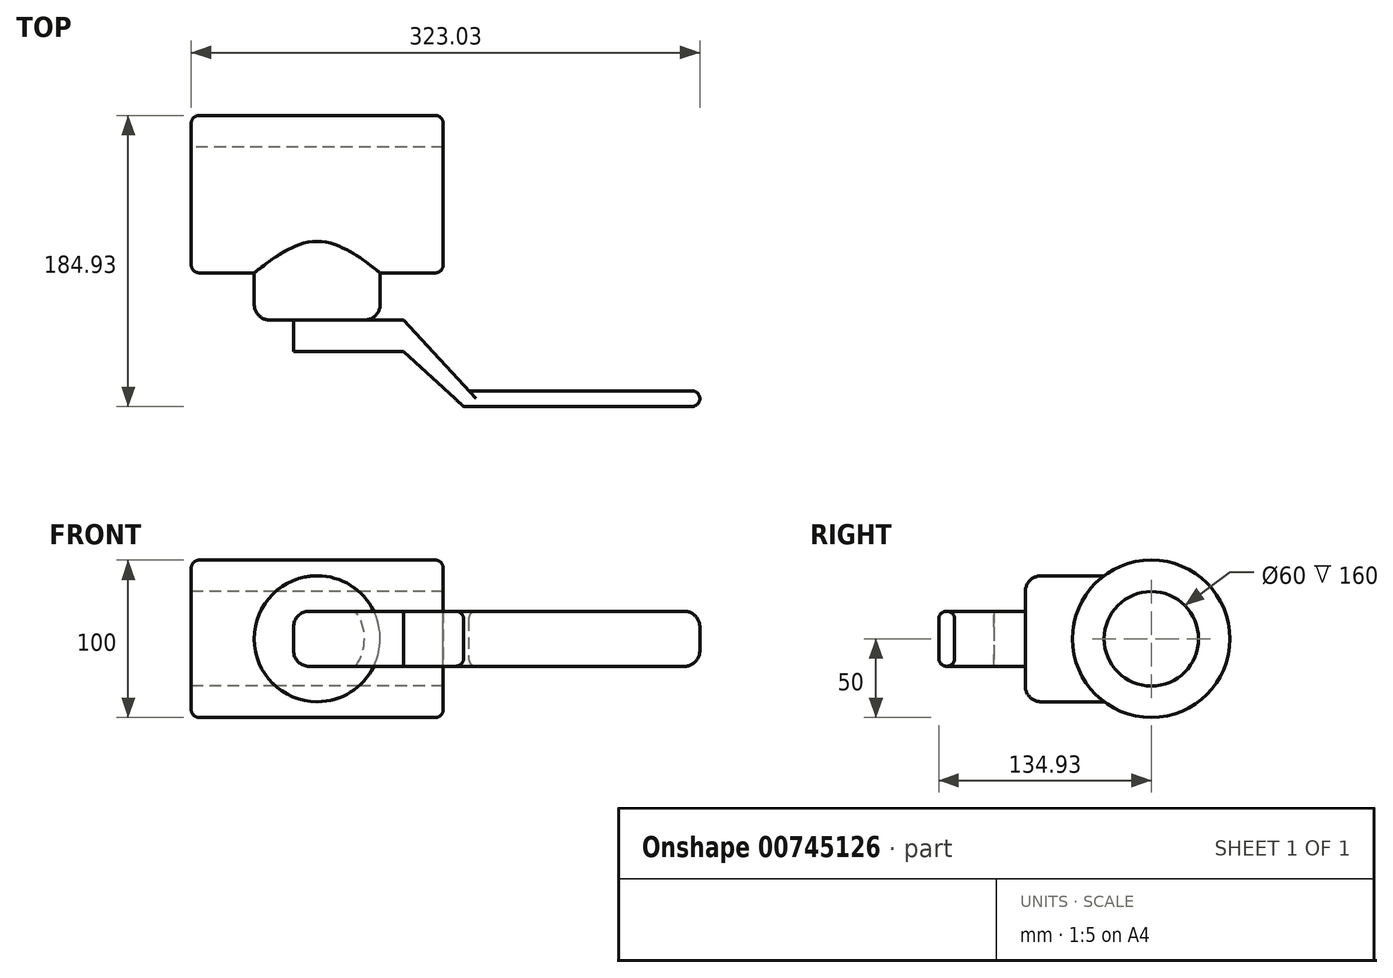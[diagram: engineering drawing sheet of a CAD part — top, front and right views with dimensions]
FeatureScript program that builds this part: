
annotation { "Feature Type Name" : "Feature", "Feature Type Description" : "" }
export const myFeature = defineFeature(function(context is Context, id is Id, definition is map)
    precondition{}
    {
        {
            var Q0;
            Q0=qCreatedBy(makeId("Right.planeOp"),FACE);
            var sketch = newSketch(context, id + "F0", { "sketchPlane" : qUnion([Q0])});
            skCircle(sketch, "E0", {"center": v(0, 0) * mm, "radius": 30 * mm});
            skCircle(sketch, "E1", {"center": v(0, 0) * mm, "radius": 50 * mm});
            skSolve(sketch);
        }
        {
            var Q0;
            Q0=makeQuery(id+"F0.imprint","IMPRINT",FACE,{"disambiguationData":[TD([[makeQuery(id+"F0.imprint","IMPRINT",EDGE,{"derivedFrom":sQuery(id+"F0.wireOp",EDGE,"E0")}),-1.0]])]});
            extrude(context, id + "F1", {"entities" : qUnion([Q0]), "depth" : 160 * mm, "offsetDistance" : 25 * mm});
        }
        {
            var Q0;
            Q0=qCreatedBy(makeId("Front.planeOp"),FACE);
            var sketch = newSketch(context, id + "F2", { "sketchPlane" : qUnion([Q0])});
            skCircle(sketch, "E2", {"center": v(80, 0) * mm, "radius": 40 * mm});
            skSolve(sketch);
        }
        {
            var Q0;
            Q0=makeQuery(id+"F2.imprint","IMPRINT",FACE,{"disambiguationData":[TD([[makeQuery(id+"F2.imprint","IMPRINT",EDGE,{"derivedFrom":sQuery(id+"F2.wireOp",EDGE,"E2")}),1.0]])]});
            var Q1;
            Q1=sQuery(id+"F2.wireOp",EDGE,"E2");
            var Q2;
            Q2=makeQuery(id+"F1.opExtrude","SWEPT_BODY",BODY,{"disambiguationData":[OSD([sQuery(id+"F0.wireOp",EDGE,"E0"),sQuery(id+"F0.wireOp",EDGE,"E1")])]});
            extrude(context, id + "F3", {"entities" : qUnion([Q0]), "operationType" : NewBodyOperationType.ADD, "surfaceEntities" : qUnion([Q1]), "depth" : 80 * mm, "offsetDistance" : 25 * mm, "hasSecondDirection" : true, "secondDirectionBound" : SecondDirectionBoundingType.UP_TO_BODY, "secondDirectionOppositeDirection" : false, "secondDirectionDepth" : 25 * mm, "secondDirectionBoundEntityBody" : qUnion([Q2])});
        }
        {
            var Q0;
            Q0=makeQuery(id+"F3.opExtrude","CAP_EDGE",EDGE,{"disambiguationData":[OSD([sQuery(id+"F2.wireOp",EDGE,"E2")])],"isStart":false});
            fillet(context, id + "F4", {"entities" : qUnion([Q0]), "radius" : 10 * mm, "tangentPropagation" : true, "allowEdgeOverflow" : false});
        }
        {
            var Q0;
            Q0=qCreatedBy(makeId("Top.planeOp"),FACE);
            var sketch = newSketch(context, id + "F5", { "sketchPlane" : qUnion([Q0])});
            skLineSegment(sketch, "E3.0", {"start": v(110, -80) * mm, "end": v(50, -80) * mm});
            skLineSegment(sketch, "E4.bottom", {"start": v(65, -80) * mm, "end": v(135, -80) * mm});
            skLineSegment(sketch, "E4.top", {"start": v(65, -100) * mm, "end": v(135, -100) * mm});
            skLineSegment(sketch, "E4.left", {"start": v(65, -80) * mm, "end": v(65, -100) * mm});
            skLineSegment(sketch, "E5", {"start": v(135, -100) * mm, "end": v(173.03, -134.93) * mm});
            skLineSegment(sketch, "E6", {"start": v(173.03, -134.93) * mm, "end": v(323.03, -134.93) * mm});
            skLineSegment(sketch, "E7", {"start": v(323.03, -134.93) * mm, "end": v(323.03, -124.93) * mm});
            skLineSegment(sketch, "E8", {"start": v(323.03, -124.93) * mm, "end": v(176.23, -124.93) * mm});
            skLineSegment(sketch, "E9", {"start": v(176.23, -124.93) * mm, "end": v(135, -80) * mm});
            skSolve(sketch);
        }
        {
            var Q0;
            Q0=makeQuery(id+"F5.imprint","IMPRINT",FACE,{"disambiguationData":[TD([[makeQuery(id+"F5.imprint","IMPRINT",EDGE,{"derivedFrom":sQuery(id+"F5.wireOp",EDGE,"E4.bottom")}),-1.0]])]});
            extrude(context, id + "F6", {"entities" : qUnion([Q0]), "operationType" : NewBodyOperationType.ADD, "endBound" : BoundingType.SYMMETRIC, "depth" : 35 * mm, "offsetDistance" : 25 * mm});
        }
        {
            var Q0;
            Q0=makeQuery(id+"F6.opExtrude","CAP_EDGE",EDGE,{"disambiguationData":[OSD([sQuery(id+"F5.wireOp",EDGE,"E4.left")])],"isStart":true});
            var Q1;
            Q1=makeQuery(id+"F6.opExtrude","CAP_EDGE",EDGE,{"disambiguationData":[OSD([sQuery(id+"F5.wireOp",EDGE,"E4.left")])],"isStart":false});
            var Q2;
            Q2=makeQuery(id+"F6.opExtrude","CAP_EDGE",EDGE,{"disambiguationData":[OSD([sQuery(id+"F5.wireOp",EDGE,"E7")])],"isStart":true});
            var Q3;
            Q3=makeQuery(id+"F6.opExtrude","CAP_EDGE",EDGE,{"disambiguationData":[OSD([sQuery(id+"F5.wireOp",EDGE,"E7")])],"isStart":false});
            fillet(context, id + "F7", {"entities" : qUnion([Q0, Q1, Q2, Q3]), "radius" : 10 * mm, "tangentPropagation" : true, "allowEdgeOverflow" : false});
        }
        {
            var Q0;
            Q0=makeQuery(id+"F6.opExtrude","CAP_EDGE",EDGE,{"disambiguationData":[OSD([sQuery(id+"F5.wireOp",EDGE,"E6")])],"isStart":true});
            var Q1;
            Q1=makeQuery(id+"F6.opExtrude","CAP_EDGE",EDGE,{"disambiguationData":[OSD([sQuery(id+"F5.wireOp",EDGE,"E8")])],"isStart":true});
            fillet(context, id + "F8", {"entities" : qUnion([Q0, Q1]), "radius" : 5 * mm, "tangentPropagation" : true, "allowEdgeOverflow" : false});
        }
        {
            var Q0;
            Q0=makeQuery(id+"F1.opExtrude","CAP_EDGE",EDGE,{"disambiguationData":[OSD([sQuery(id+"F0.wireOp",EDGE,"E1")])],"isStart":false});
            var Q1;
            Q1=makeQuery(id+"F1.opExtrude","CAP_EDGE",EDGE,{"disambiguationData":[OSD([sQuery(id+"F0.wireOp",EDGE,"E1")])],"isStart":true});
            fillet(context, id + "F9", {"entities" : qUnion([Q0, Q1]), "radius" : 5 * mm, "tangentPropagation" : true, "allowEdgeOverflow" : false});
        }
    });
